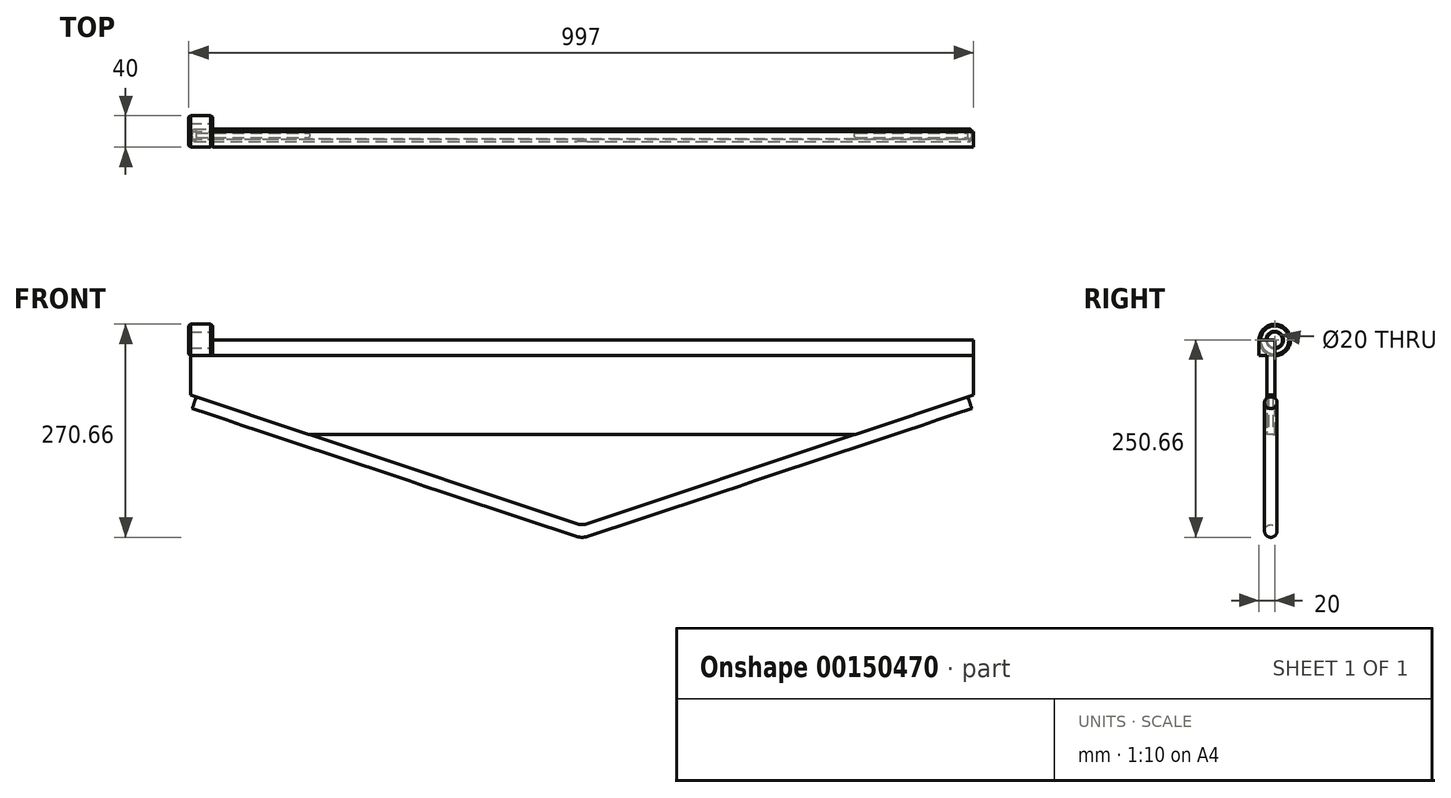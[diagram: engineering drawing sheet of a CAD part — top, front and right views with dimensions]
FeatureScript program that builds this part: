
annotation { "Feature Type Name" : "Feature", "Feature Type Description" : "" }
export const myFeature = defineFeature(function(context is Context, id is Id, definition is map)
    precondition{}
    {
        {
            var Q0;
            Q0=qCreatedBy(makeId("Front.planeOp"),FACE);
            var sketch = newSketch(context, id + "F0", { "sketchPlane" : qUnion([Q0])});
            skLineSegment(sketch, "E0.bottom", {"start": v(497.5, 60) * mm, "end": v(-497.5, 60) * mm});
            skLineSegment(sketch, "E0.top", {"start": v(497.5, -60) * mm, "end": v(-497.5, -60) * mm});
            skLineSegment(sketch, "E0.left", {"start": v(497.5, 60) * mm, "end": v(497.5, -60) * mm});
            skLineSegment(sketch, "E0.right", {"start": v(-497.5, 60) * mm, "end": v(-497.5, -60) * mm});
            skPoint(sketch, "E0.middle", {"position": v(0, 0) * mm});
            skSolve(sketch);
        }
        {
            var Q0;
            Q0=makeQuery(id+"F0.imprint","IMPRINT",FACE,{"disambiguationData":[TD([[makeQuery(id+"F0.imprint","IMPRINT",EDGE,{"derivedFrom":sQuery(id+"F0.wireOp",EDGE,"E0.bottom")}),1.0]])]});
            extrude(context, id + "F1", {"entities" : qUnion([Q0]), "depth" : 20 * mm});
        }
        {
            var Q0;
            Q0=qCreatedBy(makeId("Front.planeOp"),FACE);
            var sketch = newSketch(context, id + "F2", { "sketchPlane" : qUnion([Q0])});
            skLineSegment(sketch, "E1.bottom", {"start": v(-497.5, 60) * mm, "end": v(-469.5, 60) * mm});
            skLineSegment(sketch, "E1.top", {"start": v(-497.5, 40) * mm, "end": v(-469.5, 40) * mm});
            skLineSegment(sketch, "E1.left", {"start": v(-497.5, 60) * mm, "end": v(-497.5, 40) * mm});
            skLineSegment(sketch, "E1.right", {"start": v(-469.5, 60) * mm, "end": v(-469.5, 40) * mm});
            skSolve(sketch);
        }
        {
            var Q0;
            Q0=makeQuery(id+"F2.imprint","IMPRINT",FACE,{"disambiguationData":[TD([[makeQuery(id+"F2.imprint","IMPRINT",EDGE,{"derivedFrom":sQuery(id+"F2.wireOp",EDGE,"E1.bottom")}),-1.0]])]});
            extrude(context, id + "F3", {"entities" : qUnion([Q0]), "operationType" : NewBodyOperationType.REMOVE, "depth" : 25 * mm});
        }
        {
            var Q0;
            Q0=makeQuery(id+"F3.boolean.opBoolean","COPY",FACE,{"derivedFrom":makeQuery(id+"F3.opExtrude","SWEPT_FACE",FACE,{"disambiguationData":[OSD([sQuery(id+"F2.wireOp",EDGE,"E1.right")])]})});
            var sketch = newSketch(context, id + "F4", { "sketchPlane" : qUnion([Q0])});
            skCircle(sketch, "E2", {"center": v(0, 60) * mm, "radius": 20 * mm});
            skCircle(sketch, "E3", {"center": v(0, 60) * mm, "radius": 10 * mm});
            skSolve(sketch);
        }
        {
            var Q0;
            Q0 = qSketchRegion(id + "F4", true);
            extrude(context, id + "F5", {"entities" : qUnion([Q0]), "depth" : 30 * mm});
        }
        {
            var Q0;
            Q0=makeQuery(id+"F5.opExtrude","CAP_EDGE",EDGE,{"disambiguationData":[OSD([sQuery(id+"F4.wireOp",EDGE,"E2")])],"isStart":true});
            var Q1;
            Q1=makeQuery(id+"F5.opExtrude","CAP_EDGE",EDGE,{"disambiguationData":[OSD([sQuery(id+"F4.wireOp",EDGE,"E2")])],"isStart":false});
            chamfer(context, id + "F6", {"entities" : qUnion([Q0, Q1]), "width" : 2 * mm, "tangentPropagation" : true});
        }
        {
            var Q0;
            Q0=makeQuery(id+"F5.opExtrude","CAP_EDGE",EDGE,{"disambiguationData":[OSD([sQuery(id+"F4.wireOp",EDGE,"E3")])],"isStart":true});
            var Q1;
            Q1=makeQuery(id+"F5.opExtrude","CAP_EDGE",EDGE,{"disambiguationData":[OSD([sQuery(id+"F4.wireOp",EDGE,"E3")])],"isStart":false});
            chamfer(context, id + "F7", {"entities" : qUnion([Q0, Q1]), "width" : 1 * mm, "tangentPropagation" : true});
        }
        {
            var Q0;
            Q0=makeQuery(id+"F1.opExtrude","CAP_FACE",FACE,{"disambiguationData":[OSD([sQuery(id+"F0.wireOp",EDGE,"E0.bottom"),sQuery(id+"F0.wireOp",EDGE,"E0.top"),sQuery(id+"F0.wireOp",EDGE,"E0.left"),sQuery(id+"F0.wireOp",EDGE,"E0.right")])],"isStart":false});
            var sketch = newSketch(context, id + "F8", { "sketchPlane" : qUnion([Q0])});
            skPoint(sketch, "E4.oppositeSnap0", {"position": v(-483.5, 40) * mm});
            skLineSegment(sketch, "E4.bottom", {"start": v(-497.5, -60) * mm, "end": v(497.5, -60) * mm});
            skLineSegment(sketch, "E4.top", {"start": v(-497.5, 40) * mm, "end": v(497.5, 40) * mm});
            skLineSegment(sketch, "E4.left", {"start": v(-497.5, -60) * mm, "end": v(-497.5, 40) * mm});
            skLineSegment(sketch, "E4.right", {"start": v(497.5, -60) * mm, "end": v(497.5, 40) * mm});
            skSolve(sketch);
        }
        {
            var Q0;
            Q0=makeQuery(id+"F8.imprint","IMPRINT",FACE,{"disambiguationData":[TD([[makeQuery(id+"F8.imprint","IMPRINT",EDGE,{"derivedFrom":sQuery(id+"F8.wireOp",EDGE,"E4.bottom")}),-1.0]])]});
            extrude(context, id + "F9", {"entities" : qUnion([Q0]), "operationType" : NewBodyOperationType.REMOVE, "oppositeDirection" : true, "depth" : 10 * mm});
        }
        {
            var Q0;
            Q0=makeQuery(id+"F1.opExtrude","SWEPT_EDGE",EDGE,{"disambiguationData":[OSD([sQuery(id+"F0.wireOp",EDGE,"E0.top"),sQuery(id+"F0.wireOp",EDGE,"E0.right")])]});
            var Q1;
            Q1=makeQuery(id+"F1.opExtrude","SWEPT_EDGE",EDGE,{"disambiguationData":[OSD([sQuery(id+"F0.wireOp",EDGE,"E0.top"),sQuery(id+"F0.wireOp",EDGE,"E0.left")])]});
            chamfer(context, id + "F10", {"entities" : qUnion([Q0, Q1]), "chamferType" : ChamferType.TWO_OFFSETS, "width1" : 150 * mm, "oppositeDirection" : false, "width2" : 50 * mm, "tangentPropagation" : true});
        }
        {
            var Q0;
            Q0=qCreatedBy(makeId("Front.planeOp"),FACE);
            cPlane(context, id + "F11", {"entities" : qUnion([Q0]), "cplaneType" : CPlaneType.OFFSET, "offset" : 5 * mm, "width" : 150 * mm, "height" : 150 * mm});
        }
        {
            var Q0;
            Q0=qCreatedBy(id+"F11.planeOp",FACE);
            var sketch = newSketch(context, id + "F12", { "sketchPlane" : qUnion([Q0])});
            skLineSegment(sketch, "E5", {"start": v(-492.5, -19.57) * mm, "end": v(-6.32, -181.63) * mm});
            skLineSegment(sketch, "E6", {"start": v(6.32, -181.63) * mm, "end": v(492.5, -19.57) * mm});
            skPoint(sketch, "E7.visualSharp", {"position": v(0, -183.74) * mm});
            skArc(sketch, "E7.filletArc", {"start": v(-6.32, -181.63) * mm, "mid": v(0, -182.66) * mm, "end": v(6.32, -181.63) * mm});
            skSolve(sketch);
        }
        {
            var Q0;
            Q0=sQuery(id+"F12.wireOp",EDGE,"E5");
            var Q1;
            Q1=sQuery(id+"F12.wireOp",VERTEX,"E5.start");
            cPlane(context, id + "F13", {"entities" : qUnion([Q0, Q1]), "cplaneType" : CPlaneType.CURVE_POINT, "offset" : 25 * mm, "width" : 150 * mm, "height" : 150 * mm});
        }
        {
            var Q0;
            Q0=qCreatedBy(id+"F13.planeOp",FACE);
            var sketch = newSketch(context, id + "F14", { "sketchPlane" : qUnion([Q0])});
            skCircle(sketch, "E8", {"center": v(-5, -174.31) * mm, "radius": 8 * mm});
            skSolve(sketch);
        }
        {
            var Q0;
            Q0=makeQuery(id+"F14.imprint","IMPRINT",FACE,{"disambiguationData":[TD([[makeQuery(id+"F14.imprint","IMPRINT",EDGE,{"derivedFrom":sQuery(id+"F14.wireOp",EDGE,"E8")}),1.0]])]});
            var Q1;
            Q1=sQuery(id+"F12.wireOp",EDGE,"E5");
            var Q2;
            Q2=sQuery(id+"F12.wireOp",EDGE,"E7.filletArc");
            var Q3;
            Q3=sQuery(id+"F12.wireOp",EDGE,"E6");
            sweep(context, id + "F15", {"operationType" : NewBodyOperationType.ADD, "profiles" : qUnion([Q0]), "path" : qUnion([Q1, Q2, Q3])});
        }
    });
